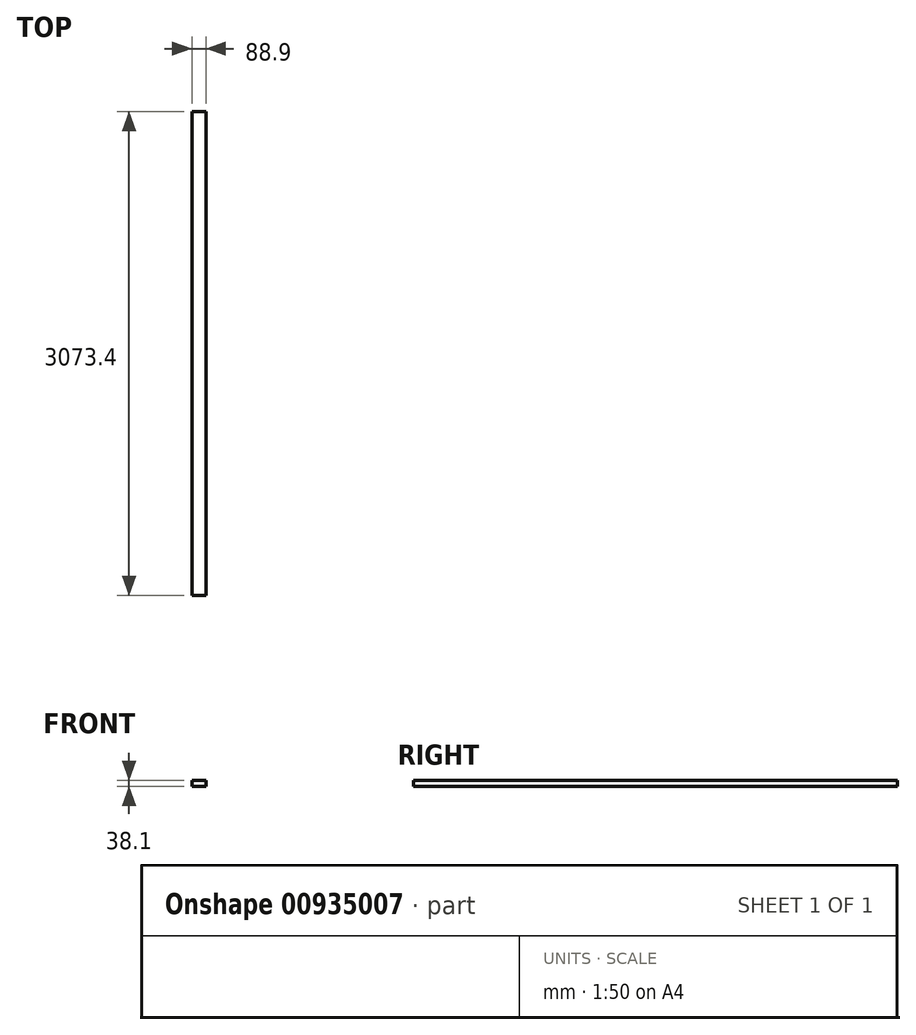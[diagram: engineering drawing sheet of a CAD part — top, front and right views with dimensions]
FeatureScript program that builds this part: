
annotation { "Feature Type Name" : "Feature", "Feature Type Description" : "" }
export const myFeature = defineFeature(function(context is Context, id is Id, definition is map)
    precondition{}
    {
        {
            var Q0;
            Q0=qCreatedBy(makeId("Front.planeOp"),FACE);
            var sketch = newSketch(context, id + "F0", { "sketchPlane" : qUnion([Q0])});
            skLineSegment(sketch, "E0.bottom", {"start": v(-44.45, 19.05) * mm, "end": v(44.45, 19.05) * mm});
            skLineSegment(sketch, "E0.top", {"start": v(-44.45, -19.05) * mm, "end": v(44.45, -19.05) * mm});
            skLineSegment(sketch, "E0.left", {"start": v(-44.45, 19.05) * mm, "end": v(-44.45, -19.05) * mm});
            skLineSegment(sketch, "E0.right", {"start": v(44.45, 19.05) * mm, "end": v(44.45, -19.05) * mm});
            skPoint(sketch, "E0.middle", {"position": v(0, 0) * mm});
            skSolve(sketch);
        }
        {
            var Q0;
            Q0 = qSketchRegion(id + "F0", true);
            extrude(context, id + "F1", {"entities" : qUnion([Q0]), "depth" : 3073.4 * mm, "offsetDistance" : 25.4 * mm, "symmetric" : true});
        }
    });
